# Revit family: Haworth_BuzziCube_SoloPouf
name_source: partatom
category: Furniture
revit_build: Autodesk Revit 2018 (Build: 20170223_1515(x64)
units: mm (PartAtom-declared; Revit-internal decimal feet)

## family parameters
Always vertical = Yes
Cut with Voids When Loaded = No
OmniClass Number = 23.40.70.14.64.21
OmniClass Title = Systems Furniture
Room Calculation Point = No
Shared = No
Work Plane-Based = No

## types (4) — shared parameters
Actual Depth = 19.69 "
Actual Height = 19.69 "
Actual Width = 19.69 "
Antiskid = No
Assembly Code = E2020200
Base Height Control = 1.05 "
Caster Finish = Haworth _ Polymer _ Slate
Casters = Yes
Manufacturer = Haworth
Model = HCBZ-CBP
Revision Number = 1
Size = Verify Final Dim. w/ Haworth
URL = http://www.haworth.com
URL - Product = https://www.haworth.com
Warranty = http://www.haworth.com
Wood Base = No
Wood Finish = Haworth _ Wood _ Collection _ Ash Natural

## per-type parameters (varying)
| type | 3D Visibility | Description | Flat | Four Squares | One Square | Sixteen Squares |
| HCBZ-CBPF-1 - Flat | No | Haworth BuzziCube - Solo Pouf - Flat | Yes | No | No | No |
| HCBZ-CBP3-101 - One Square | Yes | Haworth BuzziCube - Solo Pouf - One Square | No | No | Yes | No |
| HCBZ-CBP3-104 - Four Squares | Yes | Haworth BuzziCube - Solo Pouf - Four Squares | No | Yes | No | No |
| HCBZ-CBP3-116 - Sixteen Squares | Yes | Haworth BuzziCube - Solo Pouf - Sixteen Squares | No | No | No | Yes |

## geometry (parser evidence)
native form markers: Sweep x10
no freeform markers — native parametric forms only
